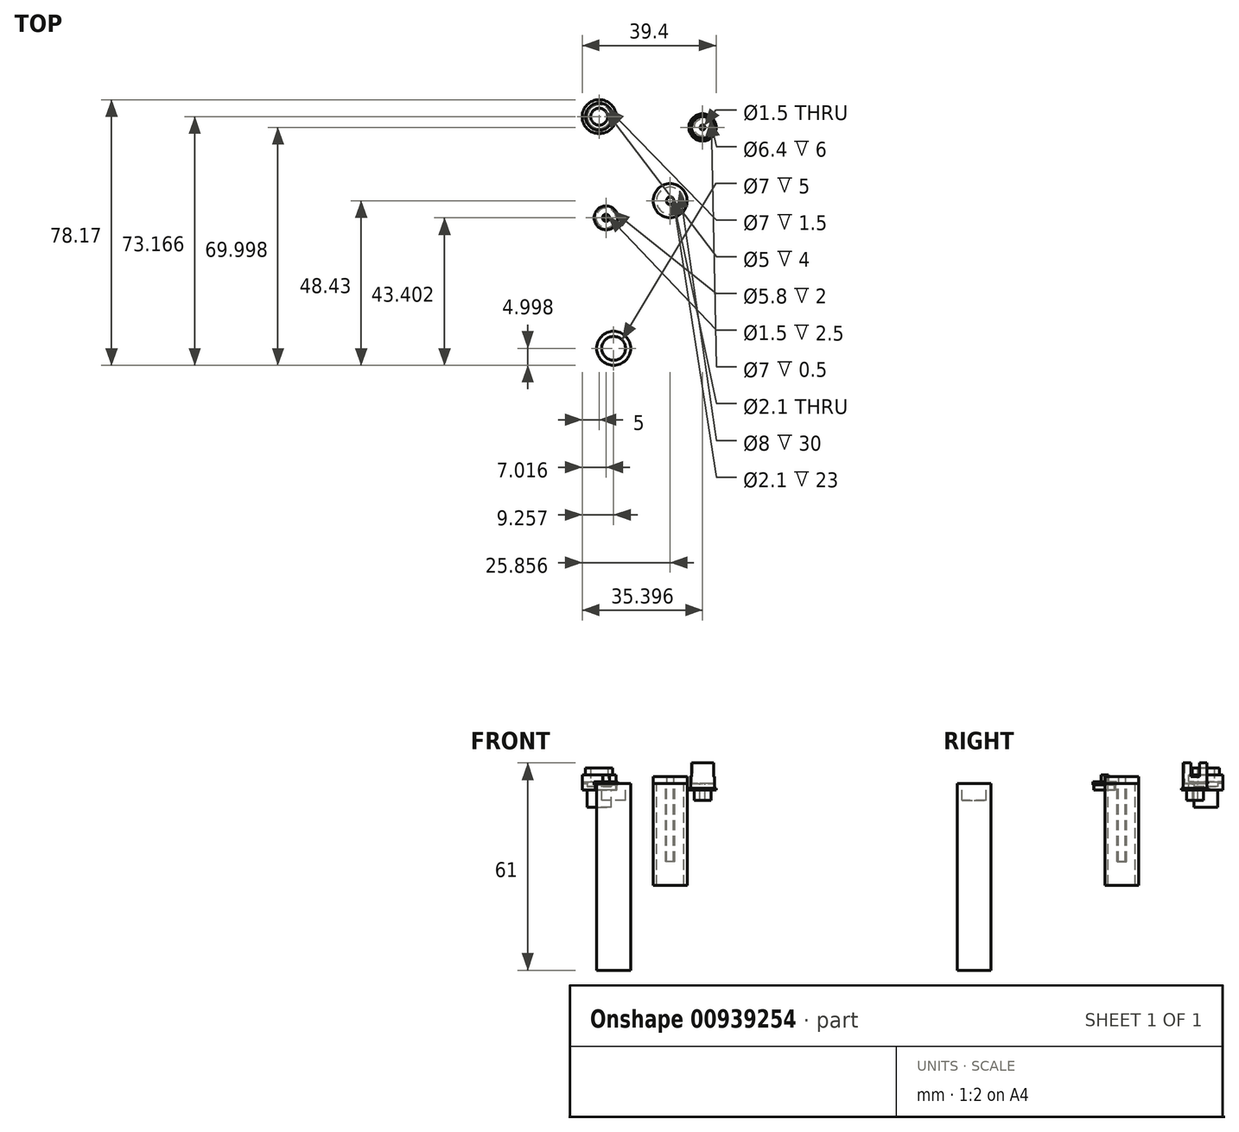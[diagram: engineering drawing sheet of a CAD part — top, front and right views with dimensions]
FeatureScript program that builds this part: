
annotation { "Feature Type Name" : "Feature", "Feature Type Description" : "" }
export const myFeature = defineFeature(function(context is Context, id is Id, definition is map)
    precondition{}
    {
        {
            var Q0;
            Q0=qCreatedBy(makeId("Top.planeOp"),FACE);
            var sketch = newSketch(context, id + "F0", { "sketchPlane" : qUnion([Q0])});
            skCircle(sketch, "E0", {"center": v(-55.86, 52.62) * mm, "radius": 5 * mm});
            skCircle(sketch, "E1", {"center": v(-55.86, 52.62) * mm, "radius": 3.5 * mm});
            skLineSegment(sketch, "E2", {"start": v(-60.83, 53.12) * mm, "end": v(-59.32, 53.12) * mm});
            skLineSegment(sketch, "E3", {"start": v(-60.83, 52.12) * mm, "end": v(-59.32, 52.12) * mm});
            skLineSegment(sketch, "E4.trimOffspring", {"start": v(-52.4, 53.12) * mm, "end": v(-50.88, 53.12) * mm});
            skLineSegment(sketch, "E5.trimOffspring", {"start": v(-52.4, 52.12) * mm, "end": v(-50.88, 52.12) * mm});
            skLineSegment(sketch, "E6.trimOffspring", {"start": v(-56.36, 49.15) * mm, "end": v(-56.36, 47.64) * mm});
            skLineSegment(sketch, "E7.trimOffspring", {"start": v(-55.36, 49.15) * mm, "end": v(-55.36, 47.64) * mm});
            skLineSegment(sketch, "E8", {"start": v(-56.36, 57.6) * mm, "end": v(-56.36, 56.08) * mm});
            skLineSegment(sketch, "E9", {"start": v(-55.36, 57.6) * mm, "end": v(-55.36, 56.08) * mm});
            skSolve(sketch);
        }
        {
            var Q0;
            {var subQ0=sQuery(id+"F0.wireOp",EDGE,"E4.trimOffspring");Q0=makeQuery(id+"F0.imprint","IMPRINT",FACE,{"disambiguationData":[TD([[makeQuery(id+"F0.imprint","IMPRINT",EDGE,{"derivedFrom":subQ0}),1.0]])]});}
            var Q1;
            {var subQ0=sQuery(id+"F0.wireOp",EDGE,"E2");Q1=makeQuery(id+"F0.imprint","IMPRINT",FACE,{"disambiguationData":[TD([[makeQuery(id+"F0.imprint","IMPRINT",EDGE,{"derivedFrom":subQ0}),-1.0]])]});}
            var Q2;
            {var subQ0=sQuery(id+"F0.wireOp",EDGE,"E6.trimOffspring");Q2=makeQuery(id+"F0.imprint","IMPRINT",FACE,{"disambiguationData":[TD([[makeQuery(id+"F0.imprint","IMPRINT",EDGE,{"derivedFrom":subQ0}),1.0]])]});}
            var Q3;
            {var subQ0=sQuery(id+"F0.wireOp",EDGE,"E5.trimOffspring");Q3=makeQuery(id+"F0.imprint","IMPRINT",FACE,{"disambiguationData":[TD([[makeQuery(id+"F0.imprint","IMPRINT",EDGE,{"derivedFrom":subQ0}),-1.0]])]});}
            var Q4;
            {var subQ0=sQuery(id+"F0.wireOp",EDGE,"E1");var subQ5=makeQuery(id+"F0.imprint","INTERSECT",VERTEX,{"derivedFrom":[subQ0,sQuery(id+"F0.wireOp",EDGE,"E4.trimOffspring")]});Q4=makeQuery(id+"F0.imprint","IMPRINT",FACE,{"disambiguationData":[TD([[makeQuery(id+"F0.imprint","IMPRINT",EDGE,{"disambiguationData":[TD([[subQ5,-1.0]])],"derivedFrom":subQ0}),1.0]])]});}
            var Q5;
            {var subQ0=sQuery(id+"F0.wireOp",EDGE,"E4.trimOffspring");Q5=makeQuery(id+"F0.imprint","IMPRINT",FACE,{"disambiguationData":[TD([[makeQuery(id+"F0.imprint","IMPRINT",EDGE,{"derivedFrom":subQ0}),-1.0]])]});}
            var Q6;
            {var subQ0=sQuery(id+"F0.wireOp",EDGE,"E3");Q6=makeQuery(id+"F0.imprint","IMPRINT",FACE,{"disambiguationData":[TD([[makeQuery(id+"F0.imprint","IMPRINT",EDGE,{"derivedFrom":subQ0}),-1.0]])]});}
            var Q7;
            {var subQ0=sQuery(id+"F0.wireOp",EDGE,"E8");Q7=makeQuery(id+"F0.imprint","IMPRINT",FACE,{"disambiguationData":[TD([[makeQuery(id+"F0.imprint","IMPRINT",EDGE,{"derivedFrom":subQ0}),1.0]])]});}
            var Q8;
            {var subQ0=sQuery(id+"F0.wireOp",EDGE,"E2");Q8=makeQuery(id+"F0.imprint","IMPRINT",FACE,{"disambiguationData":[TD([[makeQuery(id+"F0.imprint","IMPRINT",EDGE,{"derivedFrom":subQ0}),1.0]])]});}
            extrude(context, id + "F1", {"entities" : qUnion([Q0, Q1, Q2, Q3, Q4, Q5, Q6, Q7, Q8]), "oppositeDirection" : true, "depth" : 2 * mm, "offsetDistance" : 25 * mm});
        }
        {
            var Q0;
            {var subQ0=sQuery(id+"F0.wireOp",EDGE,"E1");var subQ5=makeQuery(id+"F0.imprint","INTERSECT",VERTEX,{"derivedFrom":[subQ0,sQuery(id+"F0.wireOp",EDGE,"E4.trimOffspring")]});Q0=makeQuery(id+"F0.imprint","IMPRINT",FACE,{"disambiguationData":[TD([[makeQuery(id+"F0.imprint","IMPRINT",EDGE,{"disambiguationData":[TD([[subQ5,-1.0]])],"derivedFrom":subQ0}),1.0]])]});}
            extrude(context, id + "F2", {"entities" : qUnion([Q0]), "operationType" : NewBodyOperationType.ADD, "oppositeDirection" : true, "depth" : 7 * mm, "offsetDistance" : 25 * mm});
        }
        {
            var Q0;
            {var subQ0=sQuery(id+"F0.wireOp",EDGE,"E4.trimOffspring");Q0=makeQuery(id+"F0.imprint","IMPRINT",FACE,{"disambiguationData":[TD([[makeQuery(id+"F0.imprint","IMPRINT",EDGE,{"derivedFrom":subQ0}),1.0]])]});}
            var Q1;
            {var subQ0=sQuery(id+"F0.wireOp",EDGE,"E5.trimOffspring");Q1=makeQuery(id+"F0.imprint","IMPRINT",FACE,{"disambiguationData":[TD([[makeQuery(id+"F0.imprint","IMPRINT",EDGE,{"derivedFrom":subQ0}),-1.0]])]});}
            var Q2;
            {var subQ0=sQuery(id+"F0.wireOp",EDGE,"E3");Q2=makeQuery(id+"F0.imprint","IMPRINT",FACE,{"disambiguationData":[TD([[makeQuery(id+"F0.imprint","IMPRINT",EDGE,{"derivedFrom":subQ0}),-1.0]])]});}
            var Q3;
            {var subQ0=sQuery(id+"F0.wireOp",EDGE,"E2");Q3=makeQuery(id+"F0.imprint","IMPRINT",FACE,{"disambiguationData":[TD([[makeQuery(id+"F0.imprint","IMPRINT",EDGE,{"derivedFrom":subQ0}),1.0]])]});}
            extrude(context, id + "F3", {"entities" : qUnion([Q0, Q1, Q2, Q3]), "operationType" : NewBodyOperationType.ADD, "depth" : 0.5 * mm, "offsetDistance" : 25 * mm});
        }
        {
            var Q0;
            Q0=makeQuery(id+"F3.opExtrude","CAP_FACE",FACE,{"disambiguationData":[OSD([sQuery(id+"F0.wireOp",EDGE,"E0"),sQuery(id+"F0.wireOp",EDGE,"E1"),sQuery(id+"F0.wireOp",EDGE,"E2"),sQuery(id+"F0.wireOp",EDGE,"E8")])],"isStart":false});
            var sketch = newSketch(context, id + "F4", { "sketchPlane" : qUnion([Q0])});
            skCircle(sketch, "E10", {"center": v(-55.86, 52.62) * mm, "radius": 5 * mm});
            skCircle(sketch, "E11", {"center": v(-55.86, 52.62) * mm, "radius": 2.5 * mm});
            skCircle(sketch, "E12.0", {"center": v(-55.86, 52.62) * mm, "radius": 4 * mm});
            skSolve(sketch);
        }
        {
            var Q0;
            {var subQ0=sQuery(id+"F4.wireOp",EDGE,"E10");var subQ1=makeQuery(id+"F3.opExtrude","CAP_EDGE",EDGE,{"disambiguationData":[OSD([sQuery(id+"F0.wireOp",EDGE,"E2")])],"isStart":false});var subQ2=makeQuery(id+"F4.imprint","INTERSECT",VERTEX,{"derivedFrom":[subQ1,subQ0]});Q0=makeQuery(id+"F4.imprint","IMPRINT",FACE,{"disambiguationData":[TD([[makeQuery(id+"F4.imprint","IMPRINT",EDGE,{"disambiguationData":[TD([[subQ2,1.0]])],"derivedFrom":subQ0}),1.0]])]});}
            var Q1;
            {var subQ0=sQuery(id+"F4.wireOp",EDGE,"E10");var subQ1=makeQuery(id+"F3.opExtrude","CAP_EDGE",EDGE,{"disambiguationData":[OSD([sQuery(id+"F0.wireOp",EDGE,"E2")])],"isStart":false});var subQ2=makeQuery(id+"F4.imprint","INTERSECT",VERTEX,{"derivedFrom":[subQ1,subQ0]});Q1=makeQuery(id+"F4.imprint","IMPRINT",FACE,{"disambiguationData":[TD([[makeQuery(id+"F4.imprint","IMPRINT",EDGE,{"disambiguationData":[TD([[subQ2,-1.0]])],"derivedFrom":subQ0}),1.0]])]});}
            extrude(context, id + "F5", {"entities" : qUnion([Q0, Q1]), "operationType" : NewBodyOperationType.ADD, "depth" : 2 * mm, "offsetDistance" : 25 * mm});
        }
        {
            var Q0;
            Q0=makeQuery(id+"F4.imprint","IMPRINT",FACE,{"disambiguationData":[TD([[makeQuery(id+"F4.imprint","IMPRINT",EDGE,{"derivedFrom":sQuery(id+"F4.wireOp",EDGE,"E11")}),-1.0]])]});
            var Q1;
            {var subQ1=sQuery(id+"F0.wireOp",EDGE,"E2");var subQ7=sQuery(id+"F0.wireOp",EDGE,"E1");var subQ8=makeQuery(id+"F3.opExtrude","CAP_EDGE",EDGE,{"disambiguationData":[OSD([subQ7]),TDD([makeQuery(id+"F0.imprint","IMPRINT",EDGE,{"disambiguationData":[TD([[makeQuery(id+"F0.imprint","INTERSECT",VERTEX,{"derivedFrom":[subQ7,subQ1]}),1.0]])],"derivedFrom":subQ7})])],"isStart":false});Q1=makeQuery(id+"F4.imprint","IMPRINT",FACE,{"disambiguationData":[TD([[makeQuery(id+"F4.imprint","IMPRINT",EDGE,{"derivedFrom":subQ8}),-1.0]])]});}
            extrude(context, id + "F6", {"entities" : qUnion([Q0, Q1]), "operationType" : NewBodyOperationType.ADD, "depth" : 4 * mm, "offsetDistance" : 25 * mm});
        }
        {
            var Q0;
            {var subQ0=sQuery(id+"F0.wireOp",EDGE,"E1");var subQ5=makeQuery(id+"F0.imprint","INTERSECT",VERTEX,{"derivedFrom":[subQ0,sQuery(id+"F0.wireOp",EDGE,"E4.trimOffspring")]});Q0=makeQuery(id+"F0.imprint","IMPRINT",FACE,{"disambiguationData":[TD([[makeQuery(id+"F0.imprint","IMPRINT",EDGE,{"disambiguationData":[TD([[subQ5,-1.0]])],"derivedFrom":subQ0}),1.0]])]});}
            extrude(context, id + "F7", {"entities" : qUnion([Q0]), "operationType" : NewBodyOperationType.REMOVE, "oppositeDirection" : true, "depth" : 1 * mm, "offsetDistance" : 25 * mm});
        }
        {
            var Q0;
            Q0=qCreatedBy(makeId("Top.planeOp"),FACE);
            var sketch = newSketch(context, id + "F8", { "sketchPlane" : qUnion([Q0])});
            skCircle(sketch, "E13", {"center": v(-25.46, 49.45) * mm, "radius": 3.5 * mm});
            skCircle(sketch, "E14.0", {"center": v(-25.46, 49.45) * mm, "radius": 3.2 * mm});
            skCircle(sketch, "E15", {"center": v(-25.46, 49.45) * mm, "radius": 2.5 * mm});
            skCircle(sketch, "E16", {"center": v(-25.46, 49.45) * mm, "radius": 0.75 * mm});
            skLineSegment(sketch, "E17", {"start": v(-28.73, 50.7) * mm, "end": v(-28.41, 50.7) * mm});
            skLineSegment(sketch, "E18", {"start": v(-28.73, 48.2) * mm, "end": v(-28.41, 48.2) * mm});
            skLineSegment(sketch, "E19.trimOffspring", {"start": v(-22.52, 50.7) * mm, "end": v(-22.2, 50.7) * mm});
            skLineSegment(sketch, "E20.trimOffspring", {"start": v(-22.52, 48.2) * mm, "end": v(-22.2, 48.2) * mm});
            skCircle(sketch, "E21.0", {"center": v(-25.46, 49.45) * mm, "radius": 4 * mm});
            skSolve(sketch);
        }
        {
            var Q0;
            {var subQ0=sQuery(id+"F8.wireOp",EDGE,"E17");Q0=makeQuery(id+"F8.imprint","IMPRINT",FACE,{"disambiguationData":[TD([[makeQuery(id+"F8.imprint","IMPRINT",EDGE,{"derivedFrom":subQ0}),1.0]])]});}
            var Q1;
            {var subQ0=sQuery(id+"F8.wireOp",EDGE,"E17");Q1=makeQuery(id+"F8.imprint","IMPRINT",FACE,{"disambiguationData":[TD([[makeQuery(id+"F8.imprint","IMPRINT",EDGE,{"derivedFrom":subQ0}),-1.0]])]});}
            var Q2;
            {var subQ0=sQuery(id+"F8.wireOp",EDGE,"E18");Q2=makeQuery(id+"F8.imprint","IMPRINT",FACE,{"disambiguationData":[TD([[makeQuery(id+"F8.imprint","IMPRINT",EDGE,{"derivedFrom":subQ0}),-1.0]])]});}
            var Q3;
            {var subQ0=sQuery(id+"F8.wireOp",EDGE,"E19.trimOffspring");Q3=makeQuery(id+"F8.imprint","IMPRINT",FACE,{"disambiguationData":[TD([[makeQuery(id+"F8.imprint","IMPRINT",EDGE,{"derivedFrom":subQ0}),-1.0]])]});}
            var Q4;
            Q4=makeQuery(id+"F8.imprint","IMPRINT",FACE,{"disambiguationData":[TD([[makeQuery(id+"F8.imprint","IMPRINT",EDGE,{"derivedFrom":sQuery(id+"F8.wireOp",EDGE,"E15")}),-1.0]])]});
            var Q5;
            Q5=makeQuery(id+"F8.imprint","IMPRINT",FACE,{"disambiguationData":[TD([[makeQuery(id+"F8.imprint","IMPRINT",EDGE,{"derivedFrom":sQuery(id+"F8.wireOp",EDGE,"E15")}),1.0]])]});
            extrude(context, id + "F9", {"entities" : qUnion([Q0, Q1, Q2, Q3, Q4, Q5]), "oppositeDirection" : true, "depth" : 2 * mm, "offsetDistance" : 25 * mm});
        }
        {
            var Q0;
            Q0=makeQuery(id+"F8.imprint","IMPRINT",FACE,{"disambiguationData":[TD([[makeQuery(id+"F8.imprint","IMPRINT",EDGE,{"derivedFrom":sQuery(id+"F8.wireOp",EDGE,"E15")}),1.0]])]});
            extrude(context, id + "F10", {"entities" : qUnion([Q0]), "operationType" : NewBodyOperationType.ADD, "oppositeDirection" : true, "depth" : 5 * mm, "offsetDistance" : 25 * mm});
        }
        {
            var Q0;
            {var subQ0=sQuery(id+"F8.wireOp",EDGE,"E19.trimOffspring");Q0=makeQuery(id+"F8.imprint","IMPRINT",FACE,{"disambiguationData":[TD([[makeQuery(id+"F8.imprint","IMPRINT",EDGE,{"derivedFrom":subQ0}),-1.0]])]});}
            var Q1;
            {var subQ0=sQuery(id+"F8.wireOp",EDGE,"E17");Q1=makeQuery(id+"F8.imprint","IMPRINT",FACE,{"disambiguationData":[TD([[makeQuery(id+"F8.imprint","IMPRINT",EDGE,{"derivedFrom":subQ0}),-1.0]])]});}
            extrude(context, id + "F11", {"entities" : qUnion([Q0, Q1]), "operationType" : NewBodyOperationType.ADD, "depth" : 2 * mm, "offsetDistance" : 25 * mm});
        }
        {
            var Q0;
            {var subQ0=sQuery(id+"F8.wireOp",EDGE,"E18");Q0=makeQuery(id+"F8.imprint","IMPRINT",FACE,{"disambiguationData":[TD([[makeQuery(id+"F8.imprint","IMPRINT",EDGE,{"derivedFrom":subQ0}),-1.0]])]});}
            var Q1;
            {var subQ0=sQuery(id+"F8.wireOp",EDGE,"E17");Q1=makeQuery(id+"F8.imprint","IMPRINT",FACE,{"disambiguationData":[TD([[makeQuery(id+"F8.imprint","IMPRINT",EDGE,{"derivedFrom":subQ0}),1.0]])]});}
            extrude(context, id + "F12", {"entities" : qUnion([Q0, Q1]), "operationType" : NewBodyOperationType.ADD, "depth" : 6 * mm, "offsetDistance" : 25 * mm});
        }
        {
            var Q0;
            Q0=qCreatedBy(makeId("Top.planeOp"),FACE);
            var sketch = newSketch(context, id + "F13", { "sketchPlane" : qUnion([Q0])});
            skCircle(sketch, "E22", {"center": v(-53.84, 22.85) * mm, "radius": 3.5 * mm});
            skCircle(sketch, "E23.0", {"center": v(-53.84, 22.85) * mm, "radius": 3.2 * mm});
            skCircle(sketch, "E24.0", {"center": v(-53.84, 22.85) * mm, "radius": 2.9 * mm});
            skCircle(sketch, "E25", {"center": v(-53.84, 22.85) * mm, "radius": 0.75 * mm});
            skCircle(sketch, "E26.0", {"center": v(-53.84, 22.85) * mm, "radius": 1.05 * mm});
            skSolve(sketch);
        }
        {
            var Q0;
            Q0=makeQuery(id+"F13.imprint","IMPRINT",FACE,{"disambiguationData":[TD([[makeQuery(id+"F13.imprint","IMPRINT",EDGE,{"derivedFrom":sQuery(id+"F13.wireOp",EDGE,"E23.0")}),1.0]])]});
            var Q1;
            Q1=makeQuery(id+"F13.imprint","IMPRINT",FACE,{"disambiguationData":[TD([[makeQuery(id+"F13.imprint","IMPRINT",EDGE,{"derivedFrom":sQuery(id+"F13.wireOp",EDGE,"E22")}),1.0]])]});
            extrude(context, id + "F14", {"entities" : qUnion([Q0, Q1]), "oppositeDirection" : true, "depth" : 0.5 * mm, "offsetDistance" : 25 * mm});
        }
        {
            var Q0;
            Q0=makeQuery(id+"F13.imprint","IMPRINT",FACE,{"disambiguationData":[TD([[makeQuery(id+"F13.imprint","IMPRINT",EDGE,{"derivedFrom":sQuery(id+"F13.wireOp",EDGE,"E23.0")}),1.0]])]});
            extrude(context, id + "F15", {"entities" : qUnion([Q0]), "operationType" : NewBodyOperationType.ADD, "oppositeDirection" : true, "depth" : 2 * mm, "offsetDistance" : 25 * mm});
        }
        {
            var Q0;
            Q0=makeQuery(id+"F13.imprint","IMPRINT",FACE,{"disambiguationData":[TD([[makeQuery(id+"F13.imprint","IMPRINT",EDGE,{"derivedFrom":sQuery(id+"F13.wireOp",EDGE,"E22")}),1.0]])]});
            var Q1;
            Q1=makeQuery(id+"F13.imprint","IMPRINT",FACE,{"disambiguationData":[TD([[makeQuery(id+"F13.imprint","IMPRINT",EDGE,{"derivedFrom":sQuery(id+"F13.wireOp",EDGE,"E23.0")}),1.0]])]});
            var Q2;
            Q2=makeQuery(id+"F13.imprint","IMPRINT",FACE,{"disambiguationData":[TD([[makeQuery(id+"F13.imprint","IMPRINT",EDGE,{"derivedFrom":sQuery(id+"F13.wireOp",EDGE,"E24.0")}),1.0]])]});
            extrude(context, id + "F16", {"entities" : qUnion([Q0, Q1, Q2]), "operationType" : NewBodyOperationType.ADD, "depth" : 0.5 * mm, "offsetDistance" : 25 * mm});
        }
        {
            var Q0;
            Q0=makeQuery(id+"F13.imprint","IMPRINT",FACE,{"disambiguationData":[TD([[makeQuery(id+"F13.imprint","IMPRINT",EDGE,{"derivedFrom":sQuery(id+"F13.wireOp",EDGE,"E25")}),-1.0]])]});
            extrude(context, id + "F17", {"entities" : qUnion([Q0]), "operationType" : NewBodyOperationType.ADD, "depth" : 2.5 * mm, "offsetDistance" : 25 * mm});
        }
        {
            var Q0;
            Q0=qCreatedBy(makeId("Top.planeOp"),FACE);
            var sketch = newSketch(context, id + "F18", { "sketchPlane" : qUnion([Q0])});
            skCircle(sketch, "E27", {"center": v(-35, 27.88) * mm, "radius": 5 * mm});
            skCircle(sketch, "E28.0", {"center": v(-35, 27.88) * mm, "radius": 4 * mm});
            skCircle(sketch, "E29", {"center": v(-35, 27.88) * mm, "radius": 1.05 * mm});
            skCircle(sketch, "E30.0", {"center": v(-35, 27.88) * mm, "radius": 1.35 * mm});
            skSolve(sketch);
        }
        {
            var Q0;
            Q0=makeQuery(id+"F18.imprint","IMPRINT",FACE,{"disambiguationData":[TD([[makeQuery(id+"F18.imprint","IMPRINT",EDGE,{"derivedFrom":sQuery(id+"F18.wireOp",EDGE,"E27")}),1.0]])]});
            extrude(context, id + "F19", {"entities" : qUnion([Q0]), "oppositeDirection" : true, "depth" : 30 * mm, "offsetDistance" : 25 * mm});
        }
        {
            var Q0;
            Q0=makeQuery(id+"F18.imprint","IMPRINT",FACE,{"disambiguationData":[TD([[makeQuery(id+"F18.imprint","IMPRINT",EDGE,{"derivedFrom":sQuery(id+"F18.wireOp",EDGE,"E29")}),-1.0]])]});
            extrude(context, id + "F20", {"entities" : qUnion([Q0]), "oppositeDirection" : true, "depth" : 23 * mm, "offsetDistance" : 25 * mm});
        }
        {
            var Q0;
            Q0=makeQuery(id+"F18.imprint","IMPRINT",FACE,{"disambiguationData":[TD([[makeQuery(id+"F18.imprint","IMPRINT",EDGE,{"derivedFrom":sQuery(id+"F18.wireOp",EDGE,"E27")}),1.0]])]});
            var Q1;
            Q1=makeQuery(id+"F18.imprint","IMPRINT",FACE,{"disambiguationData":[TD([[makeQuery(id+"F18.imprint","IMPRINT",EDGE,{"derivedFrom":sQuery(id+"F18.wireOp",EDGE,"E28.0")}),1.0]])]});
            var Q2;
            Q2=makeQuery(id+"F18.imprint","IMPRINT",FACE,{"disambiguationData":[TD([[makeQuery(id+"F18.imprint","IMPRINT",EDGE,{"derivedFrom":sQuery(id+"F18.wireOp",EDGE,"E29")}),-1.0]])]});
            extrude(context, id + "F21", {"entities" : qUnion([Q0, Q1, Q2]), "depth" : 2 * mm, "offsetDistance" : 25 * mm});
        }
        {
            var Q0;
            Q0=makeQuery(id+"F9.opExtrude","CAP_FACE",FACE,{"disambiguationData":[OSD([sQuery(id+"F8.wireOp",EDGE,"E13"),sQuery(id+"F8.wireOp",EDGE,"E16")])],"isStart":false});
            var sketch = newSketch(context, id + "F22", { "sketchPlane" : qUnion([Q0])});
            skCircle(sketch, "E31", {"center": v(-25.46, -49.45) * mm, "radius": 4 * mm});
            skSolve(sketch);
        }
        {
            var Q0;
            Q0=makeQuery(id+"F22.imprint","IMPRINT",FACE,{"disambiguationData":[TD([[makeQuery(id+"F22.imprint","IMPRINT",EDGE,{"derivedFrom":sQuery(id+"F22.wireOp",EDGE,"E31")}),1.0]])]});
            extrude(context, id + "F23", {"entities" : qUnion([Q0]), "oppositeDirection" : true, "depth" : 0.5 * mm, "offsetDistance" : 25 * mm});
        }
        {
            var Q0;
            Q0=qCreatedBy(makeId("Top.planeOp"),FACE);
            var sketch = newSketch(context, id + "F24", { "sketchPlane" : qUnion([Q0])});
            skCircle(sketch, "E32", {"center": v(-51.6, -15.55) * mm, "radius": 5 * mm});
            skCircle(sketch, "E33", {"center": v(-51.6, -15.55) * mm, "radius": 3.5 * mm});
            skSolve(sketch);
        }
        {
            var Q0;
            Q0=makeQuery(id+"F24.imprint","IMPRINT",FACE,{"disambiguationData":[TD([[makeQuery(id+"F24.imprint","IMPRINT",EDGE,{"derivedFrom":sQuery(id+"F24.wireOp",EDGE,"E33")}),1.0]])]});
            var Q1;
            Q1=makeQuery(id+"F24.imprint","IMPRINT",FACE,{"disambiguationData":[TD([[makeQuery(id+"F24.imprint","IMPRINT",EDGE,{"derivedFrom":sQuery(id+"F24.wireOp",EDGE,"E32")}),1.0]])]});
            extrude(context, id + "F25", {"entities" : qUnion([Q0, Q1]), "oppositeDirection" : true, "depth" : 55 * mm, "offsetDistance" : 25 * mm});
        }
        {
            var Q0;
            Q0=makeQuery(id+"F24.imprint","IMPRINT",FACE,{"disambiguationData":[TD([[makeQuery(id+"F24.imprint","IMPRINT",EDGE,{"derivedFrom":sQuery(id+"F24.wireOp",EDGE,"E33")}),1.0]])]});
            extrude(context, id + "F26", {"entities" : qUnion([Q0]), "operationType" : NewBodyOperationType.REMOVE, "oppositeDirection" : true, "depth" : 5 * mm, "offsetDistance" : 25 * mm});
        }
    });
